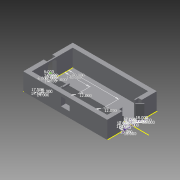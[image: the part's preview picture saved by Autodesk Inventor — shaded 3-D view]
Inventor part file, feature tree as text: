
AUTODESK INVENTOR PART (.ipt)
format: ipt  version: 2013 SP2 (Build 170200200, 200)  size: 411,648 bytes
history: native  units: in
note: dims shown in document units (in); Inventor stores cm internally (conversion verified against a paired STEP export)
features: extrude x20, sketch x12, projected_geometry x2
ambient origin geometry x8: Origin, YZ Plane, XZ Plane, XY Plane, X Axis, Y Axis, Z Axis, Center Point
feature tree (34):
  extrude  "Extrusion9"  Depth=132.0in
  extrude  "Extrusion10"  Depth=216.0in
  extrude  "Extrusion11"  Depth=24.0in
  extrude  "Extrusion12"  Depth=72.0in
  extrude  "Extrusion13"  Depth=24.0in
  extrude  "Extrusion15"  Depth=4.5in
  sketch  "Sketch15"  dims[d34=48.0in d35=114.0in]
  extrude  "Extrusion18"  Depth=168.0in
  extrude  "Extrusion19"  Depth=114.0in
  extrude  "Extrusion20"  Depth=35.0in
  extrude  "Extrusion21"  Depth=468.0in
  extrude  "Extrusion22"  Depth=1.0in TaperAngle=0.0deg
  extrude  "Extrusion23"  Depth=7.5in
  extrude  "Extrusion24"  Depth=7.25in
  extrude  "Extrusion25"  Depth=28.5in
  extrude  "Extrusion26"  Depth=7.5in
  extrude  "Extrusion27"  Depth=7.25in
  extrude  "Extrusion28"  Depth=7.5in
  extrude  "Extrusion16"  Depth=7.25in
  extrude  "Extrusion17"  Depth=7.5in
  extrude  "Extrusion14"  Depth=48.0in
  sketch  "Sketch1"  dims[d0=288.0in d1=480.0in d2=432.0in d3=240.0in d5=132.0in d7=150.0in]
  sketch  "Sketch8"  dims[d11=57.0in d17=216.0in]
  projected_geometry  "Projected Loop5"
  sketch  "Sketch9"  dims[d18=276.0in d19=24.0in]
  projected_geometry  "Projected Loop6"
  sketch  "Sketch10"  dims[d20=24.0in d23=72.0in]
  sketch  "Sketch11"  dims[d24=102.0in d25=24.0in]
  sketch  "Sketch12"  dims[d27=432.0in d28=4.5in]
  sketch  "Sketch14"  dims[d29=0.0in d30=168.0in]
  sketch  "Sketch16"  dims[d36=24.0in d46=35.0in]
  sketch  "Sketch17"  dims[d105=35.0in d106=468.0in]
  sketch  "Sketch18"  dims[d107=96.0in d108=0.0in d109=1.0in d110=0.0in]
  sketch  "Sketch19"  dims[d111=16.0in d112=0.0in d113=7.5in d115=7.25in d116=28.5in d117=7.5in d118=7.25in d119=7.5in d120=7.25in d121=7.5in d122=7.25in d123=7.5in d124=7.25in d125=7.5in d126=7.25in d127=7.5in d128=7.25in d129=7.5in d130=7.25in d131=7.5in d132=7.25in d133=7.5in d134=7.25in d135=7.5in d136=7.25in d137=7.5in d138=7.25in d139=7.5in d140=7.25in d141=7.5in d142=7.25in d143=16.0in d144=0.0in d145=48.0in d147=48.0in d148=32.0in d150=16.0in d151=0.0in d152=12.75in d153=0.0in d154=7.25in d155=7.5in d156=1.0in d158=1.0in d159=0.0in d161=12.0in d163=12.0in d164=140.0in d165=280.0in d166=12.0in d167=17.5in d168=17.5in d169=12.0in d172=17.0in d173=17.0in d174=8.5in d175=12.0in d176=17.0in d177=17.0in d178=8.5in d179=12.0in d180=17.0in d181=17.0in d182=8.5in d183=18.0in d184=18.0in d185=24.0in d186=2.0in d187=0.0in d188=3.0in d189=0.0in d190=1.0in d191=0.0in d192=6.0in d193=6.0in d194=6.0in d195=18.0in d196=18.0in d197=18.0in d198=18.0in d199=36.0in d200=6.0in d201=1.0in d202=0.0in d203=1.0in d204=0.0in d205=80.0in d206=0.0in d207=80.0in d208=0.0in d209=80.0in d210=0.0in d211=80.0in d212=0.0in d213=1.0in d214=0.0in d215=6.0in d216=36.0in d217=80.0in d218=0.0in d219=1.0in d220=0.0in d221=1.0in d222=0.0in]
